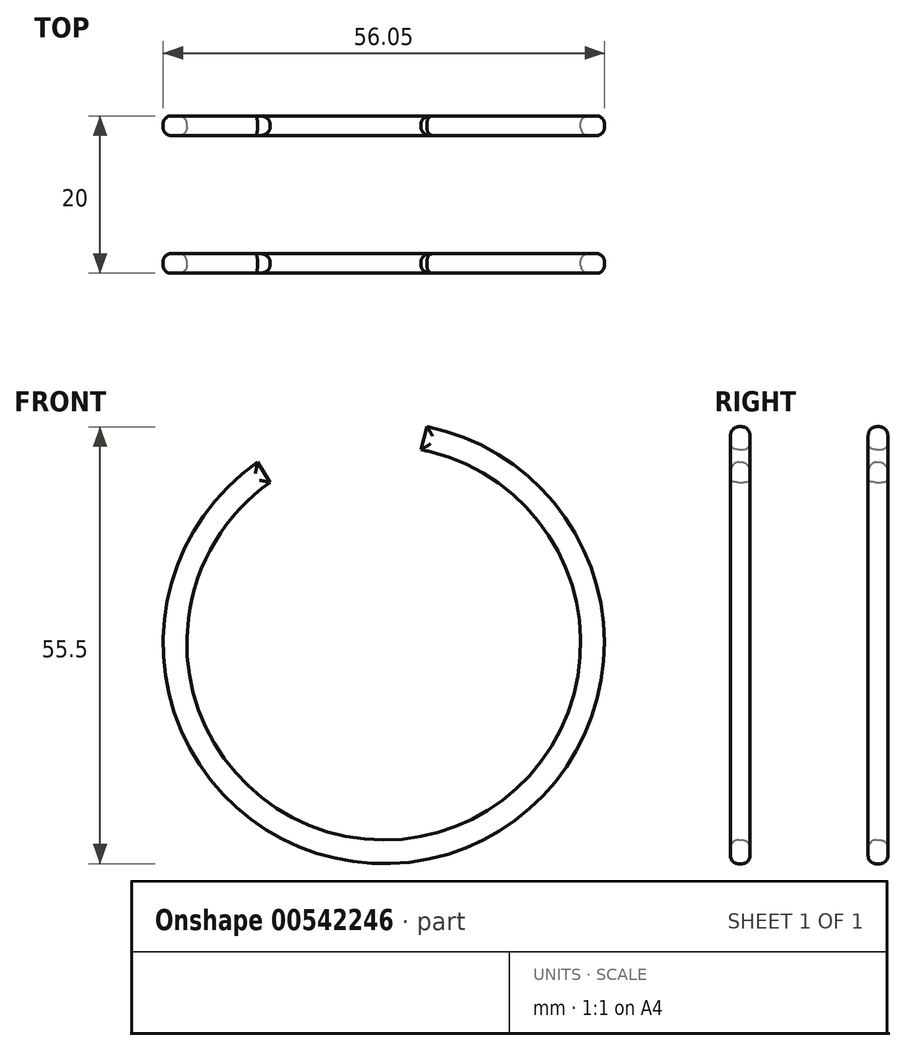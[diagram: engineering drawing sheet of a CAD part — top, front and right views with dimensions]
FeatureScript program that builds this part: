
annotation { "Feature Type Name" : "Feature", "Feature Type Description" : "" }
export const myFeature = defineFeature(function(context is Context, id is Id, definition is map)
    precondition{}
    {
        {
            var Q0;
            Q0=qCreatedBy(makeId("Front.planeOp"),FACE);
            var sketch = newSketch(context, id + "F0", { "sketchPlane" : qUnion([Q0])});
            skArc(sketch, "E0", {"start": v(-13.19, 21.24) * mm, "mid": v(5.19, -24.46) * mm, "end": v(3.43, 24.76) * mm});
            skArc(sketch, "E1.0", {"start": v(-14.77, 23.79) * mm, "mid": v(5.78, -27.45) * mm, "end": v(3.96, 27.72) * mm});
            skArc(sketch, "E2", {"start": v(-14.77, 23.79) * mm, "mid": v(-12.7, 23.3) * mm, "end": v(-13.19, 21.24) * mm});
            skArc(sketch, "E3", {"start": v(3.43, 24.76) * mm, "mid": v(2.15, 26.52) * mm, "end": v(3.96, 27.72) * mm});
            skArc(sketch, "E4", {"start": v(-14.43, 20.4) * mm, "mid": v(5.29, -24.47) * mm, "end": v(4.75, 24.54) * mm});
            skLineSegment(sketch, "E5", {"start": v(4.75, 24.54) * mm, "end": v(5.48, 27.46) * mm});
            skLineSegment(sketch, "E6", {"start": v(-14.43, 20.4) * mm, "end": v(-16.02, 22.96) * mm});
            skSolve(sketch);
        }
        {
            var Q0;
            {var subQ0=sQuery(id+"F0.wireOp",EDGE,"E2");Q0=makeQuery(id+"F0.imprint","IMPRINT",FACE,{"disambiguationData":[TD([[makeQuery(id+"F0.imprint","IMPRINT",EDGE,{"derivedFrom":subQ0}),-1.0]])]});}
            var Q1;
            {var subQ1=sQuery(id+"F0.wireOp",EDGE,"E0");var subQ8=sQuery(id+"F0.wireOp",EDGE,"E6");var subQ10=makeQuery(id+"F0.imprint","INTERSECT",VERTEX,{"derivedFrom":[subQ1,subQ8]});Q1=makeQuery(id+"F0.imprint","IMPRINT",FACE,{"disambiguationData":[TD([[makeQuery(id+"F0.imprint","IMPRINT",EDGE,{"disambiguationData":[TD([[subQ10,-1.0]])],"derivedFrom":subQ1}),-1.0]])]});}
            var Q2;
            {var subQ0=sQuery(id+"F0.wireOp",EDGE,"E3");Q2=makeQuery(id+"F0.imprint","IMPRINT",FACE,{"disambiguationData":[TD([[makeQuery(id+"F0.imprint","IMPRINT",EDGE,{"derivedFrom":subQ0}),-1.0]])]});}
            extrude(context, id + "F1", {"entities" : qUnion([Q0, Q1, Q2]), "depth" : 20 * mm, "offsetDistance" : 25 * mm});
        }
        {
            var Q0;
            {var subQ1=sQuery(id+"F0.wireOp",EDGE,"E0");var subQ8=sQuery(id+"F0.wireOp",EDGE,"E6");var subQ10=makeQuery(id+"F0.imprint","INTERSECT",VERTEX,{"derivedFrom":[subQ1,subQ8]});Q0=makeQuery(id+"F0.imprint","IMPRINT",FACE,{"disambiguationData":[TD([[makeQuery(id+"F0.imprint","IMPRINT",EDGE,{"disambiguationData":[TD([[subQ10,-1.0]])],"derivedFrom":subQ1}),-1.0]])]});}
            extrude(context, id + "F2", {"entities" : qUnion([Q0]), "operationType" : NewBodyOperationType.REMOVE, "depth" : 17.5 * mm, "offsetDistance" : 25 * mm, "hasSecondDirection" : true, "secondDirectionOppositeDirection" : false, "secondDirectionDepth" : 2.5 * mm});
        }
        {
            var Q0;
            Q0=makeQuery(id+"F2.boolean.opBoolean","COPY",FACE,{"derivedFrom":makeQuery(id+"F2.opExtrude","CAP_FACE",FACE,{"disambiguationData":[OSD([sQuery(id+"F0.wireOp",EDGE,"E0"),sQuery(id+"F0.wireOp",EDGE,"E1.0"),sQuery(id+"F0.wireOp",EDGE,"E4"),sQuery(id+"F0.wireOp",EDGE,"E5"),sQuery(id+"F0.wireOp",EDGE,"E6")])],"isStart":true})});
            var Q1;
            Q1=makeQuery(id+"F1.opExtrude","CAP_FACE",FACE,{"disambiguationData":[OSD([sQuery(id+"F0.wireOp",EDGE,"E0"),sQuery(id+"F0.wireOp",EDGE,"E1.0"),sQuery(id+"F0.wireOp",EDGE,"E2"),sQuery(id+"F0.wireOp",EDGE,"E3"),sQuery(id+"F0.wireOp",EDGE,"E4")])],"isStart":false});
            var Q2;
            Q2=makeQuery(id+"F1.opExtrude","CAP_FACE",FACE,{"disambiguationData":[OSD([sQuery(id+"F0.wireOp",EDGE,"E0"),sQuery(id+"F0.wireOp",EDGE,"E1.0"),sQuery(id+"F0.wireOp",EDGE,"E2"),sQuery(id+"F0.wireOp",EDGE,"E3"),sQuery(id+"F0.wireOp",EDGE,"E4")])],"isStart":true});
            var Q3;
            Q3=makeQuery(id+"F2.boolean.opBoolean","COPY",FACE,{"derivedFrom":makeQuery(id+"F2.opExtrude","CAP_FACE",FACE,{"disambiguationData":[OSD([sQuery(id+"F0.wireOp",EDGE,"E0"),sQuery(id+"F0.wireOp",EDGE,"E1.0"),sQuery(id+"F0.wireOp",EDGE,"E4"),sQuery(id+"F0.wireOp",EDGE,"E5"),sQuery(id+"F0.wireOp",EDGE,"E6")])],"isStart":false})});
            fillet(context, id + "F3", {"entities" : qUnion([Q0, Q1, Q2, Q3]), "radius" : 1 * mm, "tangentPropagation" : true, "allowEdgeOverflow" : false});
        }
    });
